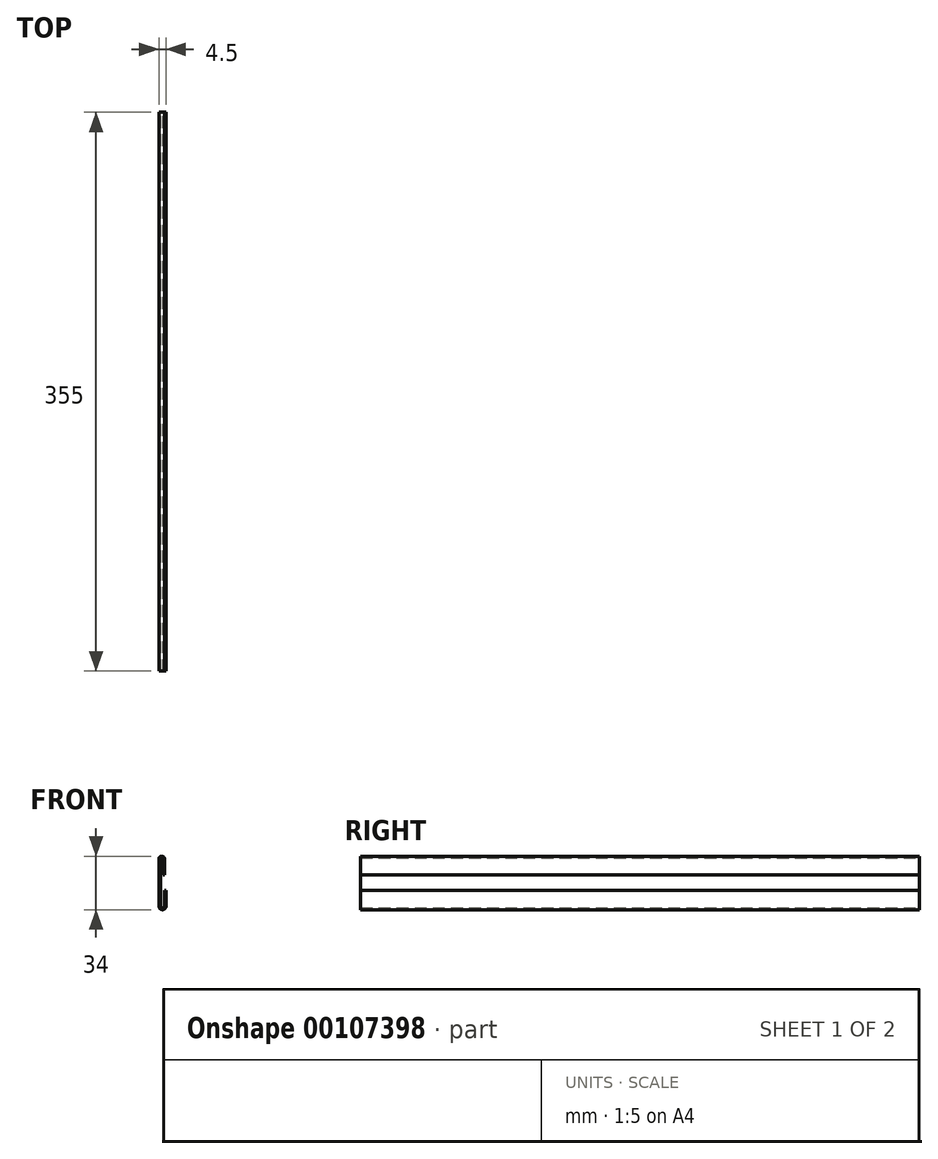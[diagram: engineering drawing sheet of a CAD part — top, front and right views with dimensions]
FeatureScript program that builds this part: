
annotation { "Feature Type Name" : "Feature", "Feature Type Description" : "" }
export const myFeature = defineFeature(function(context is Context, id is Id, definition is map)
    precondition{}
    {
        {
            var Q0;
            Q0=qCreatedBy(makeId("Front.planeOp"),FACE);
            var sketch = newSketch(context, id + "F0", { "sketchPlane" : qUnion([Q0])});
            skLineSegment(sketch, "E0", {"start": v(-2.5, -15) * mm, "end": v(-2.5, 15) * mm});
            skLineSegment(sketch, "E1", {"start": v(2, -15) * mm, "end": v(2, -5) * mm});
            skArc(sketch, "E2", {"start": v(-2.5, -15) * mm, "mid": v(-0.25, -17.25) * mm, "end": v(2, -15) * mm});
            skLineSegment(sketch, "E3.1", {"start": v(1, -15) * mm, "end": v(1, -5) * mm});
            skArc(sketch, "E3.2", {"start": v(-1.5, -15) * mm, "mid": v(-0.25, -16.25) * mm, "end": v(1, -15) * mm});
            skLineSegment(sketch, "E3.3", {"start": v(-1.5, -15) * mm, "end": v(-1.5, 15) * mm});
            skLineSegment(sketch, "E4", {"start": v(1, -5) * mm, "end": v(2, -5) * mm});
            skLineSegment(sketch, "E5", {"start": v(0, 15) * mm, "end": v(0, 5) * mm});
            skLineSegment(sketch, "E6", {"start": v(0, 5) * mm, "end": v(1, 5) * mm});
            skLineSegment(sketch, "E7", {"start": v(1, 5) * mm, "end": v(1, 15) * mm});
            skArc(sketch, "E8", {"start": v(-1.5, 15) * mm, "mid": v(-0.75, 15.75) * mm, "end": v(0, 15) * mm});
            skArc(sketch, "E9", {"start": v(-2.5, 15) * mm, "mid": v(-0.75, 16.75) * mm, "end": v(1, 15) * mm});
            skSolve(sketch);
        }
        {
            var Q0;
            Q0 = qSketchRegion(id + "F0", true);
            extrude(context, id + "F1", {"entities" : qUnion([Q0]), "depth" : 355 * mm});
        }
    });
